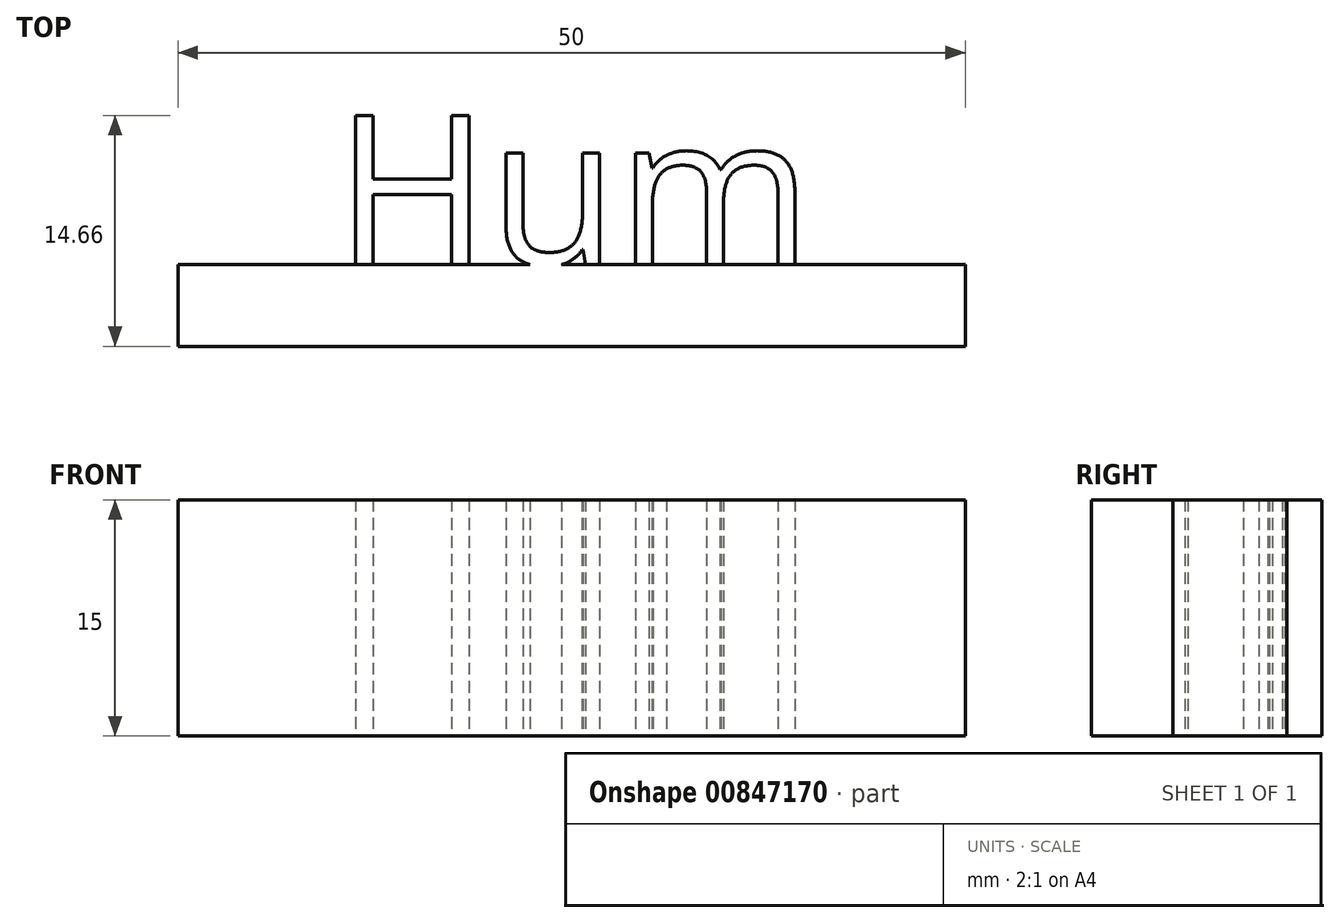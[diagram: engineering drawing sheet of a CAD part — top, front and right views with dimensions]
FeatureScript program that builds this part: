
annotation { "Feature Type Name" : "Feature", "Feature Type Description" : "" }
export const myFeature = defineFeature(function(context is Context, id is Id, definition is map)
    precondition{}
    {
        {
            var Q0;
            Q0=qCreatedBy(makeId("Top.planeOp"),FACE);
            var sketch = newSketch(context, id + "F0", { "sketchPlane" : qUnion([Q0])});
            skLineSegment(sketch, "E0.bottom", {"start": v(0, 0) * mm, "end": v(50, 0) * mm});
            skLineSegment(sketch, "E0.top", {"start": v(0, 5.19) * mm, "end": v(50, 5.19) * mm});
            skLineSegment(sketch, "E0.left", {"start": v(0, 0) * mm, "end": v(0, 5.19) * mm});
            skLineSegment(sketch, "E0.right", {"start": v(50, 0) * mm, "end": v(50, 5.19) * mm});
            skText(sketch, "E1", { "text": "Hum", "fontName": "OpenSans-Regular.ttf"});
            const initialGuessF0  = {"E1": [0.00998, 0.00519, 1, 0, 0.00955]};
            skSetInitialGuess(sketch, initialGuessF0);
            skSolve(sketch);
        }
        {
            var Q0;
            Q0 = qSketchRegion(id + "F0", true);
            extrude(context, id + "F1", {"entities" : qUnion([Q0]), "depth" : 15 * mm, "offsetDistance" : 25 * mm});
        }
    });
